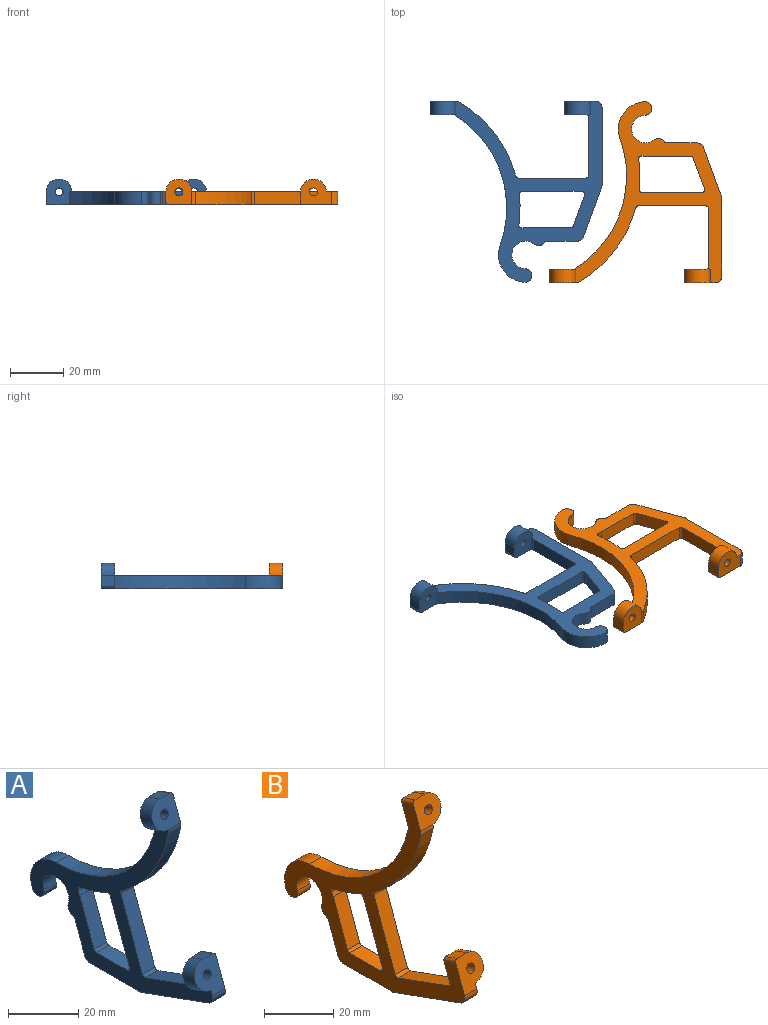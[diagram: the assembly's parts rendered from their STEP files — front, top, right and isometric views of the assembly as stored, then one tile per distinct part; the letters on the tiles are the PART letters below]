
ASSEMBLY  parts=2 mates=3
PART A: 45 faces, bbox 9.7x73.3x71.3 mm
  f0: plane 4.7x1.71mm, normal (-1,0,0), area 0mm2, adj f6,f25,f26,f31
  f1: plane 4.7x1.71mm, normal (-1,0,0), area 0mm2, adj f18,f19,f20,f30
  f2: cylinder r=46.01mm len=10.8mm, axis (-1,0,0), area 57.3mm2, adj f28,f29,f39,f42
  f3: cylinder r=10.2mm len=5mm, axis (-1,0,0), area 7.1mm2, adj f4,f28,f29,f39
  f4: plane 15.83x5.76mm, normal (0,-0.94,0.34), area 84.2mm2, adj f3,f28,f29,f40
  f5: plane 12.32x5mm, normal (0,0,1), area 61.6mm2, adj f28,f29,f40,f41
  f6: plane 10.81x9.69mm, normal (0,-0.94,0.34), area 85.6mm2, adj f0,f7,f26,f28,f29,f31,f32,f44
  f7: cylinder r=2.5mm len=5mm, axis (-1,0,0), area 19.6mm2, adj f6,f8,f28,f29
  f8: plane 27.03x9.84mm, normal (0,-0.34,-0.94), area 143.8mm2, adj f7,f9,f28,f29
  f9: cylinder r=2.5mm len=5mm, axis (-1,0,0), area 4.4mm2, adj f8,f10,f28,f29
  f10: plane 19.77x5mm, normal (0,0,-1), area 98.8mm2, adj f9,f11,f28,f29
  f11: cylinder r=2.5mm len=5mm, axis (-1,0,0), area 15.3mm2, adj f10,f12,f28,f29
  f12: plane 10.82x5mm, normal (0,0.94,-0.34), area 57.6mm2, adj f11,f28,f29,f34
  f13: cylinder r=2.5mm len=5mm, axis (-1,0,0), area 21.2mm2, adj f14,f28,f29,f34
  f14: cylinder r=5.2mm len=10.4mm, axis (-1,0,0), area 98.5mm2, adj f13,f15,f28,f29
  f15: cylinder r=2.5mm len=5mm, axis (-1,0,0), area 39.3mm2, adj f14,f16,f28,f29
  f16: cylinder r=10.2mm len=13.44mm, axis (-1,0,0), area 96.6mm2, adj f15,f17,f28,f29
  f17: cylinder r=41.01mm len=40.16mm, axis (-1,0,0), area 280.1mm2, adj f16,f28,f29,f35
  f18: plane 9.69x9.1mm, normal (0,0.94,-0.34), area 71.7mm2, adj f1,f19,f28,f29,f30,f33,f35,f43
  f19: plane 4.7x4mm, normal (0,0.34,0.94), area 20mm2, adj f1,f18,f20,f43
  f20: plane 9.69x9.11mm, normal (0,-0.94,0.34), area 76.5mm2, adj f1,f19,f21,f28,f29,f30,f33,f43
  f21: cylinder r=2.5mm len=5mm, axis (-1,0,0), area 6.6mm2, adj f20,f22,f28,f29
  f22: cylinder r=46.01mm len=29.32mm, axis (-1,0,0), area 178.6mm2, adj f21,f28,f29,f36
  f23: plane 23.77x8.65mm, normal (0,-0.94,0.34), area 126.5mm2, adj f28,f29,f36,f37
  f24: plane 20.45x7.44mm, normal (0,0.34,0.94), area 108.8mm2, adj f28,f29,f37,f38
  f25: plane 9.69x9.1mm, normal (0,0.94,-0.34), area 68.1mm2, adj f0,f26,f28,f29,f31,f32,f38,f44
  f26: plane 4.7x4mm, normal (0,0.34,0.94), area 20mm2, adj f0,f6,f25,f44
  f27: plane 21.11x7.68mm, normal (0,0.94,-0.34), area 112.3mm2, adj f28,f29,f41,f42
  f28: plane 73.34x70.37mm, normal (1,0,0), area 975.8mm2, adj f2,f3,f4,f5,f6,f7,f8,f9
  f29: plane 73.34x62.21mm, normal (-1,0,0), area 888.9mm2, adj f2,f3,f4,f5,f6,f7,f8,f9
  f30: cylinder r=4.85mm len=10.81mm, axis (0,-0.94,0.34), area 74.6mm2, adj f1,f18,f20,f29
  f31: cylinder r=4.85mm len=10.81mm, axis (0,-0.94,0.34), area 74.6mm2, adj f0,f6,f25,f29
  f32: cylinder r=1.5mm len=5.72mm, axis (0,-0.94,0.34), area 47.1mm2, adj f6,f25
  f33: cylinder r=1.5mm len=5.72mm, axis (0,-0.94,0.34), area 47.1mm2, adj f18,f20
  f34: cylinder r=1mm len=5mm, axis (-1,0,0), area 5.1mm2, adj f12,f13,f28,f29
  f35: cylinder r=1mm len=5mm, axis (-1,0,0), area 2.8mm2, adj f17,f18,f28,f29
  f36: cylinder r=1mm len=5mm, axis (-1,0,0), area 6.5mm2, adj f22,f23,f28,f29
  f37: cylinder r=1mm len=5mm, axis (-1,0,0), area 7.9mm2, adj f23,f24,f28,f29
  f38: cylinder r=1mm len=5mm, axis (-1,0,0), area 7.9mm2, adj f24,f25,f28,f29
  f39: cylinder r=1mm len=5mm, axis (1,0,0), area 9.2mm2, adj f2,f3,f28,f29
  f40: cylinder r=1mm len=5mm, axis (1,0,0), area 6.1mm2, adj f4,f5,f28,f29
  f41: cylinder r=1mm len=5mm, axis (1,0,0), area 9.6mm2, adj f5,f27,f28,f29
  f42: cylinder r=1mm len=5mm, axis (-1,0,0), area 8.4mm2, adj f2,f27,f28,f29
  f43: cylinder r=1mm len=5.04mm, axis (0,0.94,-0.34), area 7.9mm2, adj f18,f19,f20,f28
  f44: cylinder r=1mm len=5.04mm, axis (0,0.94,-0.34), area 7.9mm2, adj f6,f25,f26,f28
PART B: 45 faces, bbox 9.7x73.3x71.3 mm
  f0: plane 4.7x1.71mm, normal (1,0,0), area 0mm2, adj f6,f25,f26,f31
  f1: plane 4.7x1.71mm, normal (1,0,0), area 0mm2, adj f18,f19,f20,f30
  f2: cylinder r=46.01mm len=10.8mm, axis (1,0,0), area 57.3mm2, adj f28,f29,f39,f42
  f3: cylinder r=10.2mm len=5mm, axis (1,0,0), area 7.1mm2, adj f4,f28,f29,f39
  f4: plane 15.83x5.76mm, normal (0,-0.94,0.34), area 84.2mm2, adj f3,f28,f29,f40
  f5: plane 12.32x5mm, normal (0,0,1), area 61.6mm2, adj f28,f29,f40,f41
  f6: plane 10.81x9.69mm, normal (0,-0.94,0.34), area 85.6mm2, adj f0,f7,f26,f28,f29,f31,f32,f44
  f7: cylinder r=2.5mm len=5mm, axis (1,0,0), area 19.6mm2, adj f6,f8,f28,f29
  f8: plane 27.03x9.84mm, normal (0,-0.34,-0.94), area 143.8mm2, adj f7,f9,f28,f29
  f9: cylinder r=2.5mm len=5mm, axis (1,0,0), area 4.4mm2, adj f8,f10,f28,f29
  f10: plane 19.77x5mm, normal (0,0,-1), area 98.8mm2, adj f9,f11,f28,f29
  f11: cylinder r=2.5mm len=5mm, axis (1,0,0), area 15.3mm2, adj f10,f12,f28,f29
  f12: plane 10.82x5mm, normal (0,0.94,-0.34), area 57.6mm2, adj f11,f28,f29,f34
  f13: cylinder r=2.5mm len=5mm, axis (1,0,0), area 21.2mm2, adj f14,f28,f29,f34
  f14: cylinder r=5.2mm len=10.4mm, axis (1,0,0), area 98.5mm2, adj f13,f15,f28,f29
  f15: cylinder r=2.5mm len=5mm, axis (1,0,0), area 39.3mm2, adj f14,f16,f28,f29
  f16: cylinder r=10.2mm len=13.44mm, axis (1,0,0), area 96.6mm2, adj f15,f17,f28,f29
  f17: cylinder r=41.01mm len=40.16mm, axis (1,0,0), area 280.1mm2, adj f16,f28,f29,f35
  f18: plane 9.69x9.1mm, normal (0,0.94,-0.34), area 71.7mm2, adj f1,f19,f28,f29,f30,f33,f35,f43
  f19: plane 4.7x4mm, normal (0,0.34,0.94), area 20mm2, adj f1,f18,f20,f43
  f20: plane 9.69x9.11mm, normal (0,-0.94,0.34), area 76.5mm2, adj f1,f19,f21,f28,f29,f30,f33,f43
  f21: cylinder r=2.5mm len=5mm, axis (1,0,0), area 6.6mm2, adj f20,f22,f28,f29
  f22: cylinder r=46.01mm len=29.32mm, axis (1,0,0), area 178.6mm2, adj f21,f28,f29,f36
  f23: plane 23.77x8.65mm, normal (0,-0.94,0.34), area 126.5mm2, adj f28,f29,f36,f37
  f24: plane 20.45x7.44mm, normal (0,0.34,0.94), area 108.8mm2, adj f28,f29,f37,f38
  f25: plane 9.69x9.1mm, normal (0,0.94,-0.34), area 68.1mm2, adj f0,f26,f28,f29,f31,f32,f38,f44
  f26: plane 4.7x4mm, normal (0,0.34,0.94), area 20mm2, adj f0,f6,f25,f44
  f27: plane 21.11x7.68mm, normal (0,0.94,-0.34), area 112.3mm2, adj f28,f29,f41,f42
  f28: plane 73.34x70.37mm, normal (-1,0,0), area 975.8mm2, adj f2,f3,f4,f5,f6,f7,f8,f9
  f29: plane 73.34x62.21mm, normal (1,0,0), area 888.9mm2, adj f2,f3,f4,f5,f6,f7,f8,f9
  f30: cylinder r=4.85mm len=10.81mm, axis (0,-0.94,0.34), area 74.6mm2, adj f1,f18,f20,f29
  f31: cylinder r=4.85mm len=10.81mm, axis (0,-0.94,0.34), area 74.6mm2, adj f0,f6,f25,f29
  f32: cylinder r=1.5mm len=5.72mm, axis (0,-0.94,0.34), area 47.1mm2, adj f6,f25
  f33: cylinder r=1.5mm len=5.72mm, axis (0,-0.94,0.34), area 47.1mm2, adj f18,f20
  f34: cylinder r=1mm len=5mm, axis (1,0,0), area 5.1mm2, adj f12,f13,f28,f29
  f35: cylinder r=1mm len=5mm, axis (1,0,0), area 2.8mm2, adj f17,f18,f28,f29
  f36: cylinder r=1mm len=5mm, axis (1,0,0), area 6.5mm2, adj f22,f23,f28,f29
  f37: cylinder r=1mm len=5mm, axis (1,0,0), area 7.9mm2, adj f23,f24,f28,f29
  f38: cylinder r=1mm len=5mm, axis (1,0,0), area 7.9mm2, adj f24,f25,f28,f29
  f39: cylinder r=1mm len=5mm, axis (-1,0,0), area 9.2mm2, adj f2,f3,f28,f29
  f40: cylinder r=1mm len=5mm, axis (-1,0,0), area 6.1mm2, adj f4,f5,f28,f29
  f41: cylinder r=1mm len=5mm, axis (-1,0,0), area 9.6mm2, adj f5,f27,f28,f29
  f42: cylinder r=1mm len=5mm, axis (1,0,0), area 8.4mm2, adj f2,f27,f28,f29
  f43: cylinder r=1mm len=5.04mm, axis (0,0.94,-0.34), area 7.9mm2, adj f18,f19,f20,f28
  f44: cylinder r=1mm len=5.04mm, axis (0,0.94,-0.34), area 7.9mm2, adj f6,f25,f26,f28
PLACE A rot(axis=(-0.7,0.12,0.7),165.9deg) t=(-9.39,-80.24,118.91)mm
PLACE B rot(axis=(0.17,-0.97,0.17),91.7deg) t=(35.46,-20.8,118.91)mm
MATE parallel A.f28 <-> B.f28  axis (0,0,-1) through (-21.71,-47.26,39.91)mm
MATE parallel A.f6 <-> B.f6  axis (0,1,0) through (-2.06,-16.54,44.91)mm
MATE planar B.f28 <-> A.f28  axis (0,0,-1) through (-8,-79.35,39.91)mm
